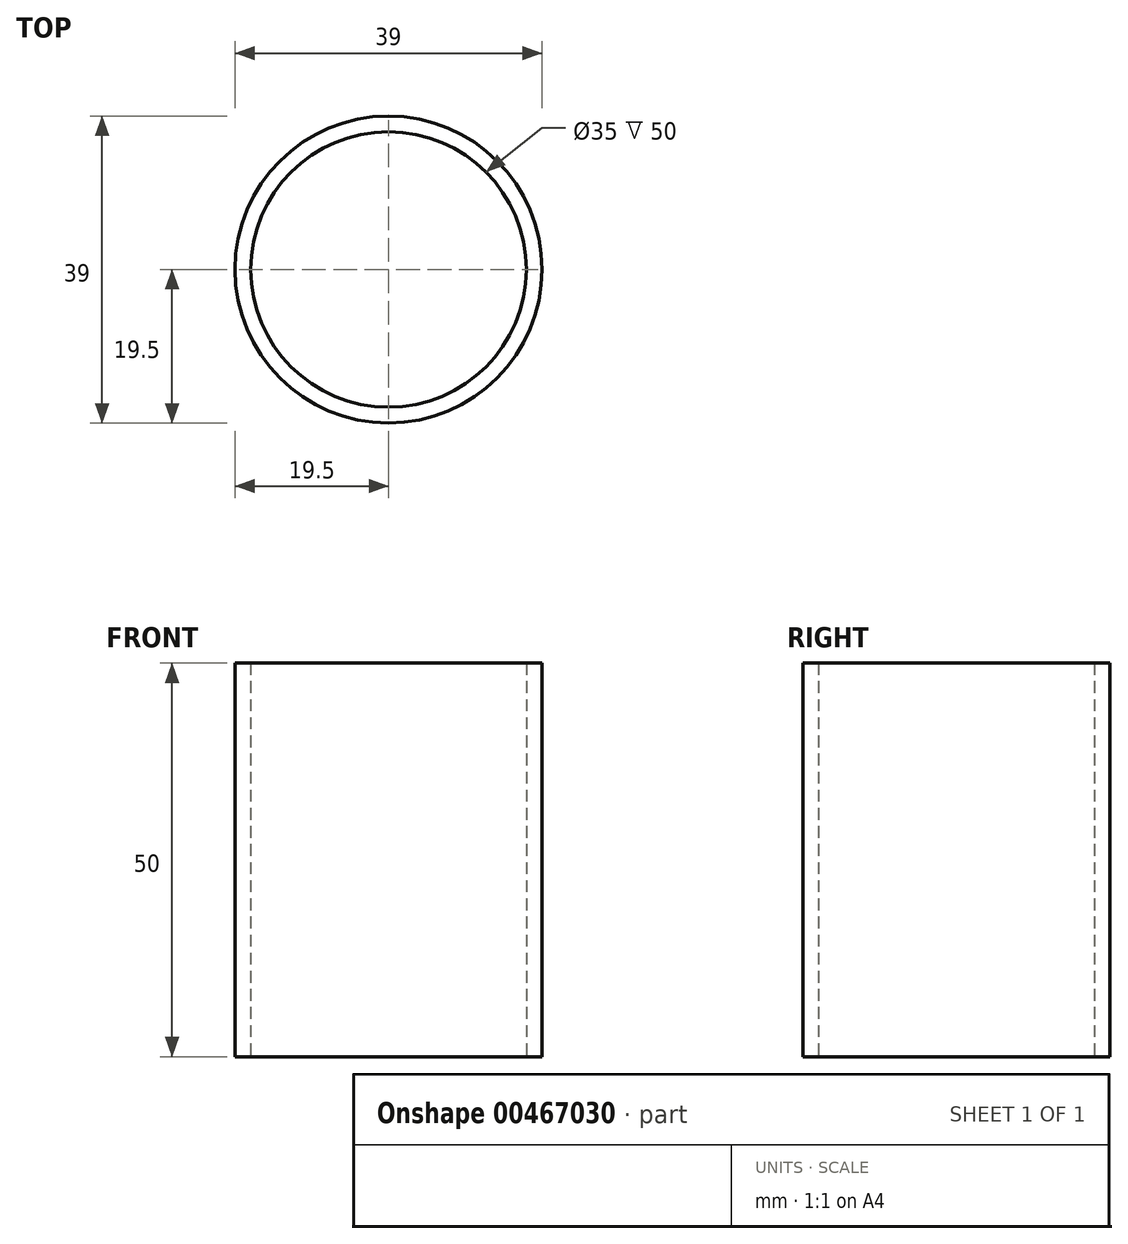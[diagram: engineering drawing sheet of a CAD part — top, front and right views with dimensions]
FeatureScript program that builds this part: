
annotation { "Feature Type Name" : "Feature", "Feature Type Description" : "" }
export const myFeature = defineFeature(function(context is Context, id is Id, definition is map)
    precondition{}
    {
        {
            var Q0;
            Q0=qCreatedBy(makeId("Top.planeOp"),FACE);
            var sketch = newSketch(context, id + "F0", { "sketchPlane" : qUnion([Q0])});
            skCircle(sketch, "E0", {"center": v(0, 0) * mm, "radius": 17.5 * mm});
            skCircle(sketch, "E1.0", {"center": v(0, 0) * mm, "radius": 19.5 * mm});
            skSolve(sketch);
        }
        {
            var Q0;
            Q0=makeQuery(id+"F0.imprint","IMPRINT",FACE,{"disambiguationData":[TD([[makeQuery(id+"F0.imprint","IMPRINT",EDGE,{"derivedFrom":sQuery(id+"F0.wireOp",EDGE,"E0")}),-1.0]])]});
            extrude(context, id + "F1", {"entities" : qUnion([Q0]), "depth" : 50 * mm});
        }
    });
